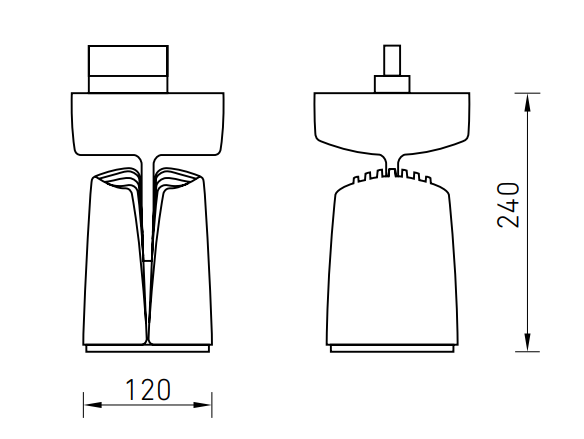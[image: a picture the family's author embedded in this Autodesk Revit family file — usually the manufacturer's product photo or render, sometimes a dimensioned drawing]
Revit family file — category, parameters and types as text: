
# Revit family: BELLT LED
name_source: partatom
category: Осветительные приборы
revit_build: Autodesk Revit 2016 (Build: 20161004_0715(x64)
units: mm (PartAtom-declared; Revit-internal decimal feet)

## family parameters
Источник света = Нет
Общий = Нет
Основа = Грань
При загрузке вырезать с полостями = Нет
Размер круглого соединителя = Использовать диаметр
Тип детали = Нормальный
Точка расчета площади = Нет

## types (1)
- BELLT LED
    ADSK_Единица измерения = Шт.
    ADSK_Завод-изготовитель = ООО МГК Световые технологии
    ADSK_Классификация нагрузок = Прочее
    ADSK_Код изделия = 1640000440
    ADSK_Количество фаз = 1
    ADSK_Количество фаз числовое = 1
    ADSK_Коэффициент мощности = 0.96
    ADSK_Масса = 2.3
    ADSK_Наименование = Cветильник с концентрирующей оптикой с установкой на шинопровод. Компактный размер, две цветовые температуры (3000К и 4000К), варианты углов рефлектора от узкого до среднего предоставляют широкие возможности для создания неповторимого и запоминающегося интерьера
    ADSK_Напряжение = 230 В
    ADSK_Номинальная мощность = 0 кВт
    ADSK_Полная мощность = 0 кВ·А
    ADSK_Размер_Высота = 240 мм
    ADSK_Размер_Длина = 245 мм
    ADSK_Размер_Ширина = 120 мм
    ADSK_Ток = 0 А
    ADSK_Энергоэффективность = 94 лм/Вт
    IP Class = IP20
    URL = https://ltcompany.com
    Блок аварийного питания = Нет
    Выбор ИС = IES BELLT LED : BELL/T LED 35 B D15 3000K
    Группа модели = Светильники
    Да = Нет
    Изготовитель = ООО МГК Световые технологии
    Класс Защиты = I
    Климатическая зона = УХЛ4
    Код по классификатору = D5020200
    Корпус = Черный металл
    Корпус X = 0 мм
    Корпус Y = 0 мм
    Нет = Нет
    Область использования = HoReCa/гостиницы/рестораны/кафе, Гипер-/супермаркеты, Культурно-развлекательные учреждения, Магазины/бутики, ТРЦ
    Описание = Cветильник с концентрирующей оптикой с установкой на шинопровод. Компактный размер, две цветовые температуры (3000К и 4000К), варианты углов рефлектора от узкого до среднего предоставляют широкие возможности для создания неповторимого и запоминающегося интерьера
    Отметка по умолчанию = 0 мм
    Плафон = Плафон самосвечение
    Полная установленная мощность = 0 кВ·А
    Пропорция = 12 мм
    Смещение ИС = 110 мм
    Тип ИС = LED
    Тип ПРА = Драйвер
    Тип продукции = Светильник
    Толщина основания = 100 мм

## geometry (parser evidence)
native form markers: Blend x26
no freeform markers — native parametric forms only
